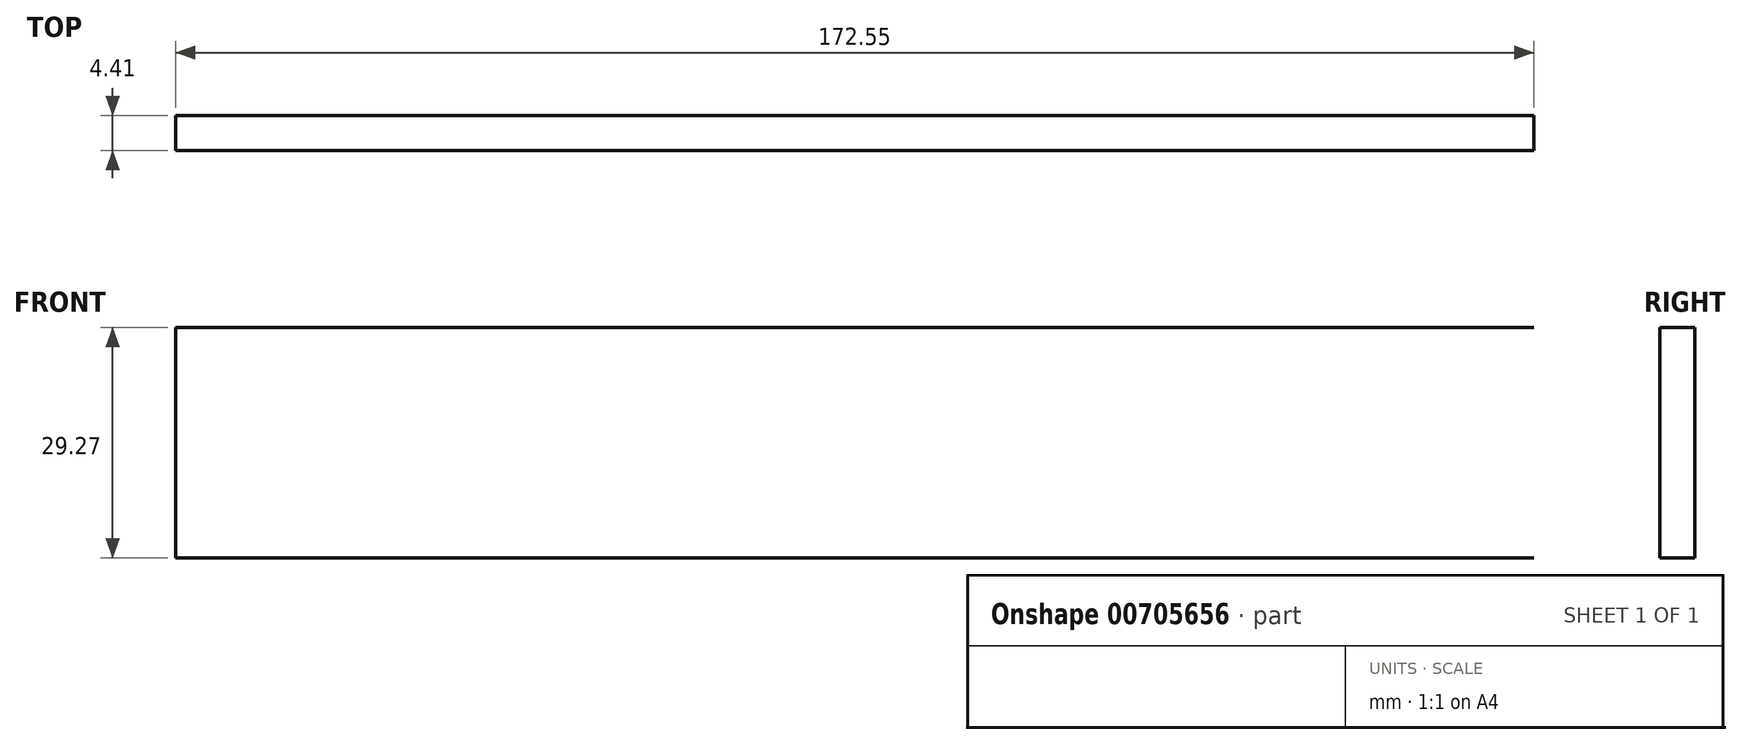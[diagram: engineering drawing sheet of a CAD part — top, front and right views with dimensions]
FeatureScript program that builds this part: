
annotation { "Feature Type Name" : "Feature", "Feature Type Description" : "" }
export const myFeature = defineFeature(function(context is Context, id is Id, definition is map)
    precondition{}
    {
        {
            var Q0;
            Q0=qCreatedBy(makeId("Front.planeOp"),FACE);
            var sketch = newSketch(context, id + "F0", { "sketchPlane" : qUnion([Q0])});
            skLineSegment(sketch, "E0.bottom", {"start": v(0, 0) * mm, "end": v(57.68, 0) * mm});
            skLineSegment(sketch, "E0.top", {"start": v(0, 58.54) * mm, "end": v(57.68, 58.54) * mm});
            skLineSegment(sketch, "E0.left", {"start": v(0, 0) * mm, "end": v(0, 58.54) * mm});
            skLineSegment(sketch, "E0.right", {"start": v(57.68, 0) * mm, "end": v(57.68, 58.54) * mm});
            skLineSegment(sketch, "E1.bottom", {"start": v(-114.87, 0) * mm, "end": v(57.68, 0) * mm});
            skLineSegment(sketch, "E1.top", {"start": v(-114.87, 29.27) * mm, "end": v(57.68, 29.27) * mm});
            skLineSegment(sketch, "E1.left", {"start": v(-114.87, 0) * mm, "end": v(-114.87, 29.27) * mm});
            skLineSegment(sketch, "E1.right", {"start": v(57.68, 0) * mm, "end": v(57.68, 29.27) * mm});
            skLineSegment(sketch, "E2.bottom", {"start": v(57.68, 14.63) * mm, "end": v(57.68, 14.63) * mm});
            skLineSegment(sketch, "E2.top", {"start": v(57.68, 0) * mm, "end": v(57.68, 0) * mm});
            skLineSegment(sketch, "E2.left", {"start": v(57.68, 14.63) * mm, "end": v(57.68, 0) * mm});
            skLineSegment(sketch, "E2.right", {"start": v(57.68, 14.63) * mm, "end": v(57.68, 0) * mm});
            skLineSegment(sketch, "E3.bottom", {"start": v(-114.43, -9.13) * mm, "end": v(-59.15, -9.13) * mm, "construction": true});
            skLineSegment(sketch, "E3.top", {"start": v(-114.43, -44.85) * mm, "end": v(-59.15, -44.85) * mm, "construction": true});
            skLineSegment(sketch, "E3.left", {"start": v(-114.43, -9.13) * mm, "end": v(-114.43, -44.85) * mm, "construction": true});
            skLineSegment(sketch, "E3.right", {"start": v(-59.15, -9.13) * mm, "end": v(-59.15, -44.85) * mm, "construction": true});
            skSolve(sketch);
        }
        {
            var Q0;
            Q0=sQuery(id+"F0.wireOp",EDGE,"E1.bottom");
            var Q1;
            Q1=sQuery(id+"F0.wireOp",EDGE,"E1.top");
            var Q2;
            Q2=sQuery(id+"F0.wireOp",EDGE,"E1.left");
            extrude(context, id + "F1", {"bodyType" : ToolBodyType.SURFACE, "surfaceEntities" : qUnion([Q0, Q1, Q2]), "depth" : 4.4 * mm, "offsetDistance" : 25 * mm});
        }
    });
